# Revit family: BR-AV2
name_source: partatom
category: Устройства связи
revit_build: Autodesk Revit 2016 (Build: 20160314_0715(x64)
units: mm (PartAtom-declared; Revit-internal decimal feet)

## family parameters
Всегда вертикально = Нет
На основе рабочей плоскости = Да
Общий = Да
При загрузке вырезать с полостями = Нет
Размер круглого соединителя = Использовать диаметр
Сохранять ориентацию аннотаций = Нет
Тип детали = Нормальный
Точка расчета площади = Нет

## types (1)
- BR-AV2
    ADSK_URL страницы изделия = https://www.bas-ip.ru
    ADSK_Версия Revit = Revit 2016
    ADSK_Единица измерения = шт
    ADSK_Завод-изготовитель = BAS-IP
    ADSK_Марка = BR-AV2
    ADSK_Наименование = КРОНШТЕЙН BR-AV2
    ADSK_Наименование краткое = BR-AV2
    ADSK_Размер_Длина = 103 мм
    ADSK_Размер_Толщина = 80 мм
    ADSK_Размер_Ширина = 161 мм
    BIM library = https://bimlib.ru
    URL = https://www.bas-ip.ru
    Группа модели = Кронштейн
    Изготовитель = BAS-IP
    Изображение типоразмера = <Нет>
    Материал корпуса = SHV_Краска Черная
    Описание = Кронштейн для накладного монтажа с козырьком для индивидуальных панелей AV-02, AV-02FP, AV-02IC.
    Отметка по умолчанию = 0 мм
    Размер = 161х103х80 мм
    Цвет = Черный
